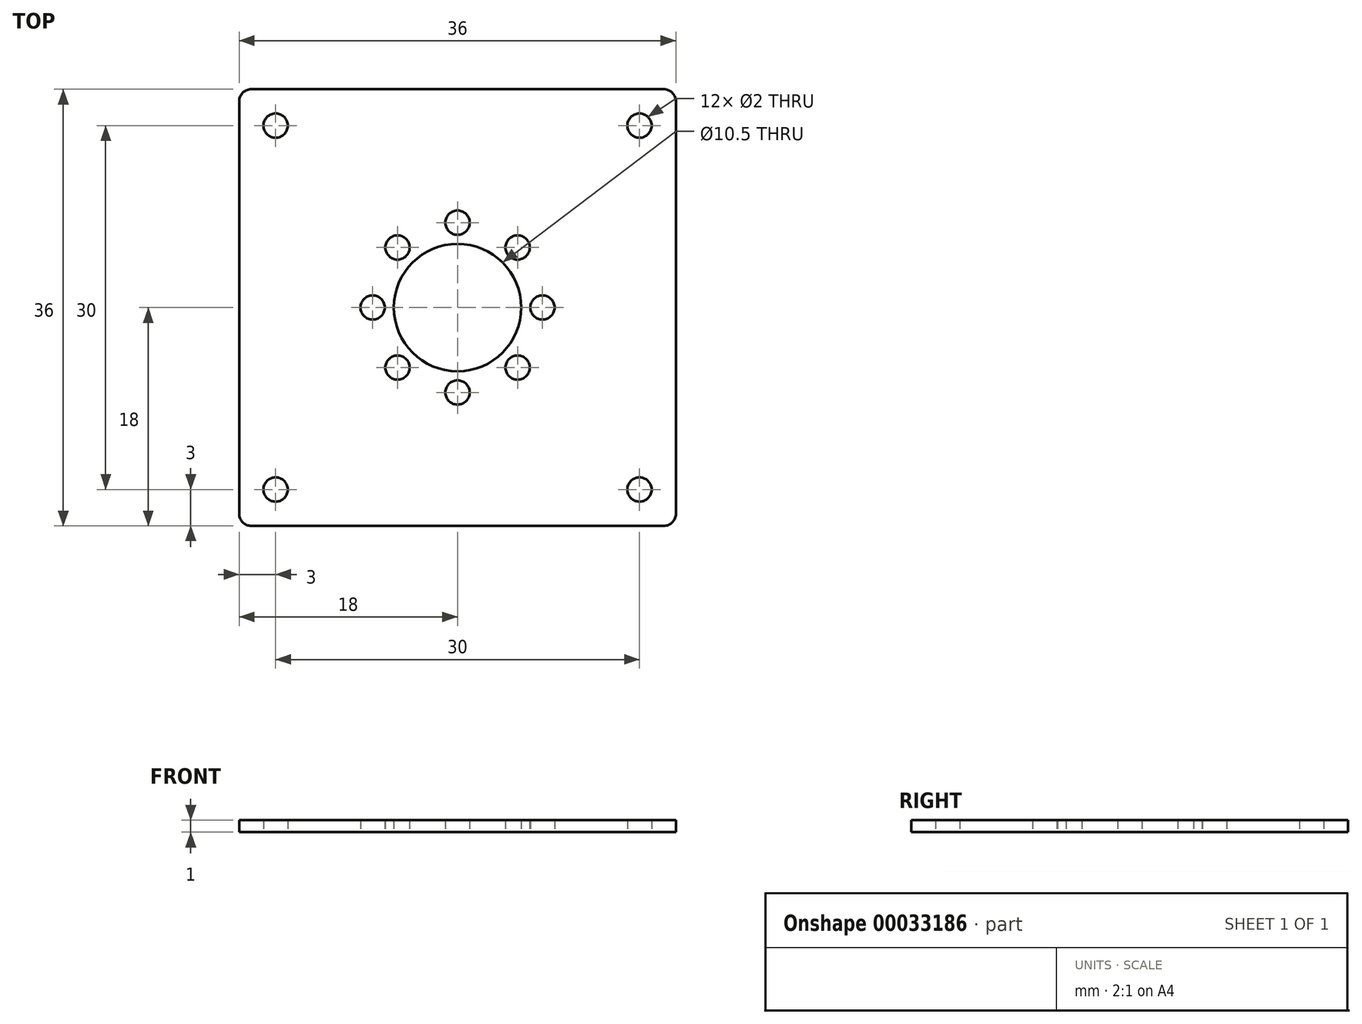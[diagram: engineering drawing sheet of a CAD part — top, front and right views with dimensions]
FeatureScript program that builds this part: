
annotation { "Feature Type Name" : "Feature", "Feature Type Description" : "" }
export const myFeature = defineFeature(function(context is Context, id is Id, definition is map)
    precondition{}
    {
        {
            var Q0;
            Q0=qCreatedBy(makeId("Top.planeOp"),FACE);
            var sketch = newSketch(context, id + "F0", { "sketchPlane" : qUnion([Q0])});
            skLineSegment(sketch, "E0.bottom", {"start": v(18, -18) * mm, "end": v(-18, -18) * mm});
            skLineSegment(sketch, "E0.top", {"start": v(18, 18) * mm, "end": v(-18, 18) * mm});
            skLineSegment(sketch, "E0.left", {"start": v(18, -18) * mm, "end": v(18, 18) * mm});
            skLineSegment(sketch, "E0.right", {"start": v(-18, -18) * mm, "end": v(-18, 18) * mm});
            skPoint(sketch, "E0.middle", {"position": v(0, 0) * mm});
            skCircle(sketch, "E1", {"center": v(-15, 15) * mm, "radius": 1 * mm});
            skCircle(sketch, "E2", {"center": v(0, 0) * mm, "radius": 5.25 * mm});
            skCircle(sketch, "E3", {"center": v(0, -7) * mm, "radius": 1 * mm});
            skCircle(sketch, "E4.1.0", {"center": v(4.95, -4.95) * mm, "radius": 1 * mm});
            skCircle(sketch, "E4.2.0", {"center": v(7, 0) * mm, "radius": 1 * mm});
            skCircle(sketch, "E4.3.0", {"center": v(4.95, 4.95) * mm, "radius": 1 * mm});
            skCircle(sketch, "E4.4.0", {"center": v(0, 7) * mm, "radius": 1 * mm});
            skCircle(sketch, "E4.5.0", {"center": v(-4.95, 4.95) * mm, "radius": 1 * mm});
            skCircle(sketch, "E4.6.0", {"center": v(-7, 0) * mm, "radius": 1 * mm});
            skCircle(sketch, "E4.7.0", {"center": v(-4.95, -4.95) * mm, "radius": 1 * mm});
            skCircle(sketch, "E5.MirrorC", {"center": v(-15, -15) * mm, "radius": 1 * mm});
            skCircle(sketch, "E6.MirrorC", {"center": v(15, 15) * mm, "radius": 1 * mm});
            skCircle(sketch, "E7.MirrorC", {"center": v(15, -15) * mm, "radius": 1 * mm});
            skSolve(sketch);
        }
        {
            var Q0;
            Q0 = qSketchRegion(id + "F0", true);
            extrude(context, id + "F1", {"entities" : qUnion([Q0]), "depth" : 1 * mm});
        }
        {
            var Q0;
            Q0=makeQuery(id+"F1.opExtrude","SWEPT_EDGE",EDGE,{"disambiguationData":[OSD([sQuery(id+"F0.wireOp",EDGE,"E0.top"),sQuery(id+"F0.wireOp",EDGE,"E0.right")])]});
            var Q1;
            Q1=makeQuery(id+"F1.opExtrude","SWEPT_EDGE",EDGE,{"disambiguationData":[OSD([sQuery(id+"F0.wireOp",EDGE,"E0.top"),sQuery(id+"F0.wireOp",EDGE,"E0.left")])]});
            var Q2;
            Q2=makeQuery(id+"F1.opExtrude","SWEPT_EDGE",EDGE,{"disambiguationData":[OSD([sQuery(id+"F0.wireOp",EDGE,"E0.bottom"),sQuery(id+"F0.wireOp",EDGE,"E0.right")])]});
            var Q3;
            Q3=makeQuery(id+"F1.opExtrude","SWEPT_EDGE",EDGE,{"disambiguationData":[OSD([sQuery(id+"F0.wireOp",EDGE,"E0.bottom"),sQuery(id+"F0.wireOp",EDGE,"E0.left")])]});
            fillet(context, id + "F2", {"entities" : qUnion([Q0, Q1, Q2, Q3]), "radius" : 1 * mm, "tangentPropagation" : true, "allowEdgeOverflow" : false});
        }
    });
